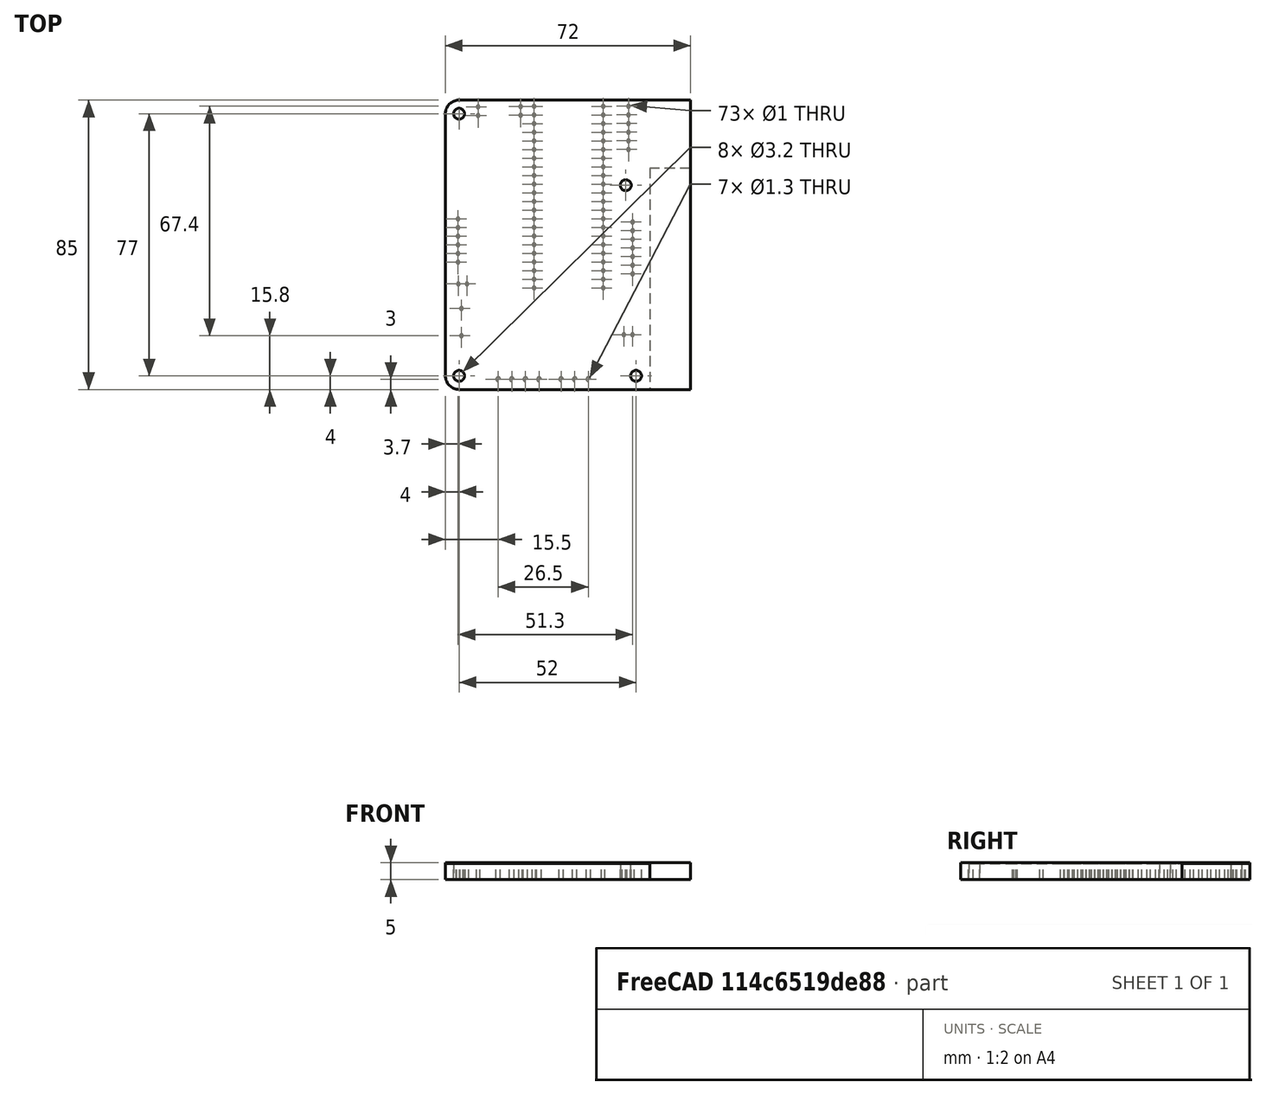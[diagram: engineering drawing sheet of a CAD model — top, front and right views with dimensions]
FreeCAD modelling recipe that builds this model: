
FCSTD DOCUMENT  (FreeCAD 0.18.4R)
Label: GbSwitchFp
License: All rights reserved
LicenseURL: http://en.wikipedia.org/wiki/All_rights_reserved
objects: Part::Feature×1, Sketcher::SketchObject×1, Part::Extrusion×1
note: 3 computed .brp shape members not serialized (recipe doc carries the construction recipe); baked Part::Feature solids carry a one-line shape summary decoded from their .brp

FEATURE [Part::Feature] Solid  label="GbSwitchFp 1"
  shape: bbox 72 x 85 x 4.69 mm, 94 faces (baked)
FEATURE [Sketcher::SketchObject] Sketch
  ExternalGeometry = -> [Solid]
  MapMode = 2
  Support = -> [Solid]
  sketch-geometry (10):
    g0: Circle CenterX=4 CenterY=-4 CenterZ=0 NormalX=0 NormalY=0 NormalZ=1 AngleXU=0 Radius=1.6
    g1: Circle CenterX=53 CenterY=-25 CenterZ=0 NormalX=0 NormalY=0 NormalZ=1 AngleXU=0 Radius=1.6
    g2: Circle CenterX=4 CenterY=-81 CenterZ=0 NormalX=0 NormalY=0 NormalZ=1 AngleXU=0 Radius=1.6
    g3: Circle CenterX=56 CenterY=-81 CenterZ=0 NormalX=0 NormalY=0 NormalZ=1 AngleXU=0 Radius=1.6
    g4: LineSegment StartX=0 StartY=-4 StartZ=0 EndX=0 EndY=-81 EndZ=0
    g5: LineSegment StartX=4 StartY=-85 StartZ=0 EndX=72 EndY=-85 EndZ=0
    g6: LineSegment StartX=4 StartY=0 StartZ=0 EndX=72 EndY=0 EndZ=0
    g7: LineSegment StartX=72 StartY=0 StartZ=0 EndX=72 EndY=-85 EndZ=0
    g8: ArcOfCircle CenterX=4 CenterY=-4 CenterZ=0 NormalX=0 NormalY=0 NormalZ=1 AngleXU=0 Radius=4 StartAngle=1.5708 EndAngle=3.14159
    g9: ArcOfCircle CenterX=4 CenterY=-81 CenterZ=0 NormalX=0 NormalY=0 NormalZ=1 AngleXU=0 Radius=4 StartAngle=3.14159 EndAngle=4.71239
  constraints (15):
    c: Coincident(g0,g-9)
    c: Coincident(g1,g-10)
    c: Coincident(g2,g-11)
    c: Coincident(g3,g-12)
    c: Coincident(g4,g-7)
    c: Coincident(g4,g-6)
    c: Coincident(g5,g-5)
    c: Coincident(g6,g-8)
    c: Coincident(g6,g-8)
    c: Coincident(g7,g6)
    c: Coincident(g7,g5)
    c: Coincident(g8,g6)
    c: Coincident(g8,g4)
    c: Coincident(g5,g9)
    c: Coincident(g9,g4)
FEATURE [Part::Extrusion] Extrude
  Base = -> Sketch
  Dir = (0,0,1)
  DirMode = 2
  FaceMakerClass = Part::FaceMakerBullseye
  LengthFwd = 5
  LengthRev = 0
  Solid = true
  Symmetric = false
